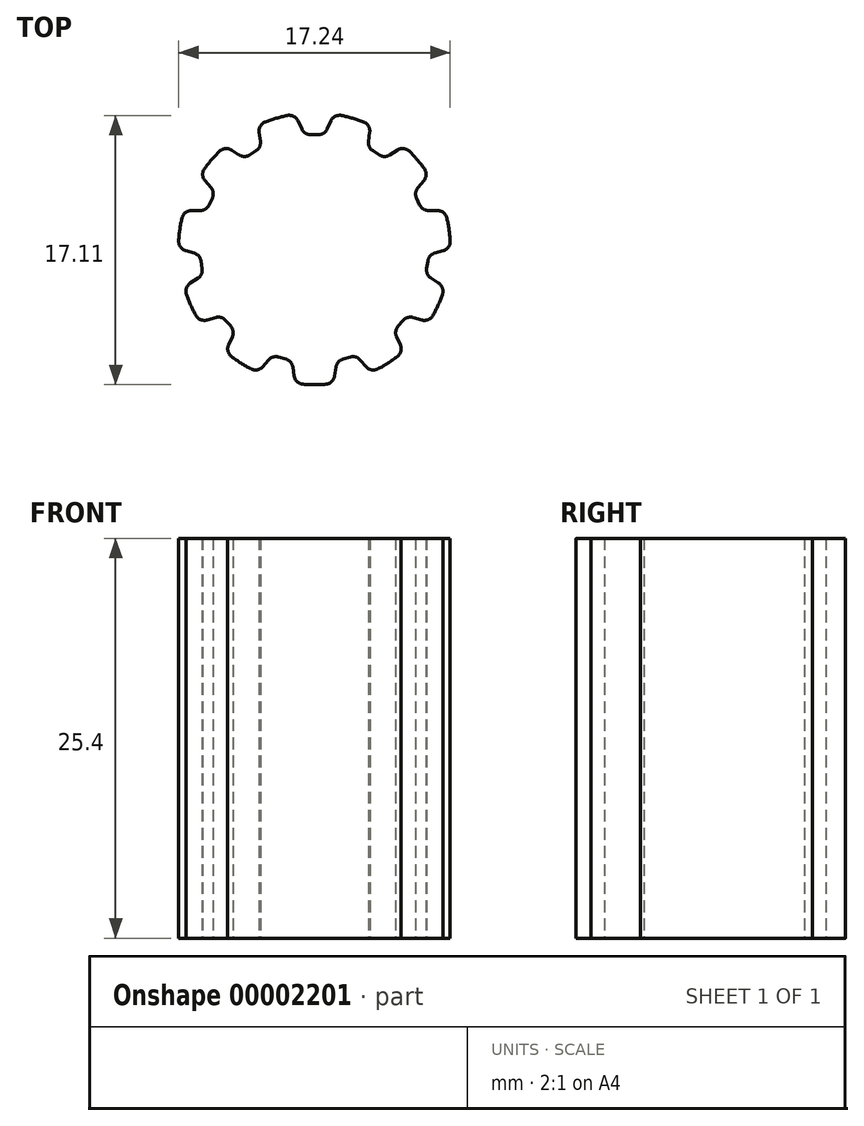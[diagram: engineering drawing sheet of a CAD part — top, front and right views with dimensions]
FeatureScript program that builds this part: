
annotation { "Feature Type Name" : "Feature", "Feature Type Description" : "" }
export const myFeature = defineFeature(function(context is Context, id is Id, definition is map)
    precondition{}
    {
        {
            var Q0;
            Q0=qCreatedBy(makeId("Top.planeOp"),FACE);
            var sketch = newSketch(context, id + "F0", { "sketchPlane" : qUnion([Q0])});
            skArc(sketch, "E0.0.1", {"start": v(8.19, -0.12) * mm, "mid": v(8.51, 0.11) * mm, "end": v(8.62, 0.5) * mm});
            skArc(sketch, "E0.0.3", {"start": v(8.19, -0.12) * mm, "mid": v(8.51, 0.11) * mm, "end": v(8.62, 0.5) * mm});
            skArc(sketch, "E1.1.1", {"start": v(8.41, 1.95) * mm, "mid": v(8.55, 1.23) * mm, "end": v(8.62, 0.5) * mm});
            skArc(sketch, "E1.1.3", {"start": v(8.41, 1.95) * mm, "mid": v(8.55, 1.23) * mm, "end": v(8.62, 0.5) * mm});
            skArc(sketch, "E1.2.1", {"start": v(8.41, 1.95) * mm, "mid": v(8.2, 2.29) * mm, "end": v(7.82, 2.42) * mm});
            skArc(sketch, "E1.2.3", {"start": v(8.41, 1.95) * mm, "mid": v(8.2, 2.29) * mm, "end": v(7.82, 2.42) * mm});
            skArc(sketch, "E1.4.1", {"start": v(6.69, 2.78) * mm, "mid": v(6.91, 2.52) * mm, "end": v(7.24, 2.43) * mm});
            skArc(sketch, "E1.4.3", {"start": v(6.69, 2.78) * mm, "mid": v(6.91, 2.52) * mm, "end": v(7.24, 2.43) * mm});
            skArc(sketch, "E1.6.1", {"start": v(6.57, 3.88) * mm, "mid": v(6.43, 3.57) * mm, "end": v(6.48, 3.23) * mm});
            skArc(sketch, "E1.6.3", {"start": v(6.57, 3.88) * mm, "mid": v(6.43, 3.57) * mm, "end": v(6.48, 3.23) * mm});
            skArc(sketch, "E1.8.1", {"start": v(6.95, 4.33) * mm, "mid": v(7.1, 4.7) * mm, "end": v(6.98, 5.08) * mm});
            skArc(sketch, "E1.8.3", {"start": v(6.95, 4.33) * mm, "mid": v(7.1, 4.7) * mm, "end": v(6.98, 5.08) * mm});
            skArc(sketch, "E1.9.1", {"start": v(6.02, 6.19) * mm, "mid": v(6.53, 5.66) * mm, "end": v(6.98, 5.08) * mm});
            skArc(sketch, "E1.9.3", {"start": v(6.02, 6.19) * mm, "mid": v(6.53, 5.66) * mm, "end": v(6.98, 5.08) * mm});
            skArc(sketch, "E1.10.1", {"start": v(6.02, 6.19) * mm, "mid": v(5.66, 6.36) * mm, "end": v(5.27, 6.27) * mm});
            skArc(sketch, "E1.10.3", {"start": v(6.02, 6.19) * mm, "mid": v(5.66, 6.36) * mm, "end": v(5.27, 6.27) * mm});
            skArc(sketch, "E1.11.1", {"start": v(4.12, 5.96) * mm, "mid": v(4.45, 5.86) * mm, "end": v(4.78, 5.95) * mm});
            skArc(sketch, "E1.11.3", {"start": v(4.12, 5.96) * mm, "mid": v(4.45, 5.86) * mm, "end": v(4.78, 5.95) * mm});
            skArc(sketch, "E1.13.1", {"start": v(3.43, 6.82) * mm, "mid": v(3.48, 6.48) * mm, "end": v(3.7, 6.22) * mm});
            skArc(sketch, "E1.13.3", {"start": v(3.43, 6.82) * mm, "mid": v(3.48, 6.48) * mm, "end": v(3.7, 6.22) * mm});
            skArc(sketch, "E1.15.1", {"start": v(3.51, 7.4) * mm, "mid": v(3.43, 7.8) * mm, "end": v(3.13, 8.05) * mm});
            skArc(sketch, "E1.15.3", {"start": v(3.51, 7.4) * mm, "mid": v(3.43, 7.8) * mm, "end": v(3.13, 8.05) * mm});
            skArc(sketch, "E1.16.1", {"start": v(1.72, 8.46) * mm, "mid": v(2.43, 8.29) * mm, "end": v(3.13, 8.05) * mm});
            skArc(sketch, "E1.16.3", {"start": v(1.72, 8.46) * mm, "mid": v(2.43, 8.29) * mm, "end": v(3.13, 8.05) * mm});
            skArc(sketch, "E1.17.1", {"start": v(1.72, 8.46) * mm, "mid": v(1.33, 8.4) * mm, "end": v(1.05, 8.12) * mm});
            skArc(sketch, "E1.17.3", {"start": v(1.72, 8.46) * mm, "mid": v(1.33, 8.4) * mm, "end": v(1.05, 8.12) * mm});
            skArc(sketch, "E1.19.1", {"start": v(0.25, 7.24) * mm, "mid": v(0.57, 7.33) * mm, "end": v(0.8, 7.6) * mm});
            skArc(sketch, "E1.19.3", {"start": v(0.25, 7.24) * mm, "mid": v(0.57, 7.33) * mm, "end": v(0.8, 7.6) * mm});
            skLineSegment(sketch, "E2.0", {"start": v(7.24, 2.43) * mm, "end": v(7.82, 2.42) * mm});
            skLineSegment(sketch, "E3.0", {"start": v(6.48, 3.23) * mm, "end": v(6.69, 2.78) * mm});
            skLineSegment(sketch, "E4.0", {"start": v(6.95, 4.33) * mm, "end": v(6.57, 3.88) * mm});
            skLineSegment(sketch, "E5.0", {"start": v(3.7, 6.22) * mm, "end": v(4.12, 5.96) * mm});
            skPoint(sketch, "E6.0", {"position": v(3.43, 6.82) * mm});
            skLineSegment(sketch, "E7.0", {"start": v(3.51, 7.4) * mm, "end": v(3.43, 6.82) * mm});
            skLineSegment(sketch, "E8.0", {"start": v(4.78, 5.95) * mm, "end": v(5.27, 6.27) * mm});
            skLineSegment(sketch, "E9.0", {"start": v(0, 7.24) * mm, "end": v(0.25, 7.24) * mm});
            skLineSegment(sketch, "E10.0", {"start": v(0.8, 7.6) * mm, "end": v(1.05, 8.12) * mm});
            skArc(sketch, "E11.0", {"start": v(7.63, -0.29) * mm, "mid": v(7.34, -0.48) * mm, "end": v(7.2, -0.79) * mm});
            skLineSegment(sketch, "E12.0", {"start": v(8.19, -0.12) * mm, "end": v(7.63, -0.29) * mm});
            skLineSegment(sketch, "E13.0", {"start": v(7.2, -0.79) * mm, "end": v(7.13, -1.27) * mm});
            skArc(sketch, "E14.0", {"start": v(7.13, -1.27) * mm, "mid": v(7.18, -1.61) * mm, "end": v(7.4, -1.87) * mm});
            skLineSegment(sketch, "E15.0", {"start": v(7.4, -1.87) * mm, "end": v(7.9, -2.2) * mm});
            skArc(sketch, "E16.0", {"start": v(8.13, -2.9) * mm, "mid": v(8.14, -2.5) * mm, "end": v(7.9, -2.2) * mm});
            skArc(sketch, "E17.0", {"start": v(8.13, -2.9) * mm, "mid": v(7.86, -3.59) * mm, "end": v(7.52, -4.24) * mm});
            skArc(sketch, "E18.0", {"start": v(6.82, -4.53) * mm, "mid": v(7.22, -4.5) * mm, "end": v(7.52, -4.24) * mm});
            skLineSegment(sketch, "E19.0", {"start": v(6.82, -4.53) * mm, "end": v(6.26, -4.37) * mm});
            skArc(sketch, "E20.0", {"start": v(6.26, -4.37) * mm, "mid": v(5.92, -4.37) * mm, "end": v(5.63, -4.55) * mm});
            skLineSegment(sketch, "E21.0", {"start": v(5.63, -4.55) * mm, "end": v(5.3, -4.93) * mm});
            skArc(sketch, "E22.0", {"start": v(5.3, -4.93) * mm, "mid": v(5.17, -5.24) * mm, "end": v(5.21, -5.57) * mm});
            skLineSegment(sketch, "E23.0", {"start": v(5.21, -5.57) * mm, "end": v(5.45, -6.11) * mm});
            skArc(sketch, "E24.0", {"start": v(5.27, -6.84) * mm, "mid": v(5.49, -6.5) * mm, "end": v(5.45, -6.11) * mm});
            skArc(sketch, "E25.0", {"start": v(5.27, -6.84) * mm, "mid": v(4.67, -7.27) * mm, "end": v(4.04, -7.64) * mm});
            skArc(sketch, "E26.0", {"start": v(3.3, -7.5) * mm, "mid": v(3.64, -7.7) * mm, "end": v(4.04, -7.64) * mm});
            skArc(sketch, "E27.0", {"start": v(2.9, -7.06) * mm, "mid": v(2.62, -6.88) * mm, "end": v(2.28, -6.88) * mm});
            skLineSegment(sketch, "E28.0", {"start": v(3.3, -7.5) * mm, "end": v(2.9, -7.06) * mm});
            skLineSegment(sketch, "E29.0", {"start": v(2.28, -6.88) * mm, "end": v(1.8, -7.02) * mm});
            skArc(sketch, "E30.0", {"start": v(1.8, -7.02) * mm, "mid": v(1.52, -7.2) * mm, "end": v(1.37, -7.5) * mm});
            skLineSegment(sketch, "E31.0", {"start": v(1.37, -7.5) * mm, "end": v(1.28, -8.09) * mm});
            skArc(sketch, "E32.0", {"start": v(0.73, -8.6) * mm, "mid": v(1.1, -8.44) * mm, "end": v(1.28, -8.09) * mm});
            skArc(sketch, "E33.0", {"start": v(0.73, -8.6) * mm, "mid": v(0.37, -8.63) * mm, "end": v(0, -8.64) * mm});
            skArc(sketch, "E34.2.MirrorCS", {"start": v(-1.72, 8.46) * mm, "mid": v(-2.43, 8.29) * mm, "end": v(-3.13, 8.05) * mm});
            skArc(sketch, "E34.3.MirrorCS", {"start": v(-8.41, 1.95) * mm, "mid": v(-8.55, 1.23) * mm, "end": v(-8.62, 0.5) * mm});
            skArc(sketch, "E34.4.MirrorCS", {"start": v(-3.43, 6.82) * mm, "mid": v(-3.48, 6.48) * mm, "end": v(-3.7, 6.22) * mm});
            skArc(sketch, "E34.5.MirrorCS", {"start": v(-1.72, 8.46) * mm, "mid": v(-1.33, 8.4) * mm, "end": v(-1.05, 8.12) * mm});
            skArc(sketch, "E34.6.MirrorCS", {"start": v(-4.12, 5.96) * mm, "mid": v(-4.45, 5.86) * mm, "end": v(-4.78, 5.95) * mm});
            skArc(sketch, "E34.7.MirrorCS", {"start": v(-8.19, -0.12) * mm, "mid": v(-8.51, 0.11) * mm, "end": v(-8.62, 0.5) * mm});
            skArc(sketch, "E34.8.MirrorCS", {"start": v(-6.57, 3.88) * mm, "mid": v(-6.43, 3.57) * mm, "end": v(-6.48, 3.23) * mm});
            skArc(sketch, "E34.9.MirrorCS", {"start": v(-3.51, 7.4) * mm, "mid": v(-3.43, 7.8) * mm, "end": v(-3.13, 8.05) * mm});
            skArc(sketch, "E34.10.MirrorCS", {"start": v(-6.69, 2.78) * mm, "mid": v(-6.91, 2.52) * mm, "end": v(-7.24, 2.43) * mm});
            skArc(sketch, "E34.11.MirrorCS", {"start": v(-6.02, 6.19) * mm, "mid": v(-6.53, 5.66) * mm, "end": v(-6.98, 5.08) * mm});
            skArc(sketch, "E34.12.MirrorCS", {"start": v(-6.02, 6.19) * mm, "mid": v(-5.66, 6.36) * mm, "end": v(-5.27, 6.27) * mm});
            skArc(sketch, "E34.13.MirrorCS", {"start": v(-6.95, 4.33) * mm, "mid": v(-7.1, 4.7) * mm, "end": v(-6.98, 5.08) * mm});
            skArc(sketch, "E34.14.MirrorCS", {"start": v(-8.41, 1.95) * mm, "mid": v(-8.2, 2.29) * mm, "end": v(-7.82, 2.42) * mm});
            skArc(sketch, "E34.15.MirrorCS", {"start": v(-8.13, -2.9) * mm, "mid": v(-7.86, -3.59) * mm, "end": v(-7.52, -4.24) * mm});
            skLineSegment(sketch, "E34.16.MirrorCS", {"start": v(-7.4, -1.87) * mm, "end": v(-7.9, -2.2) * mm});
            skPoint(sketch, "E34.18.MirrorP", {"position": v(-3.43, 6.82) * mm});
            skLineSegment(sketch, "E34.19.MirrorCS", {"start": v(-6.82, -4.53) * mm, "end": v(-6.26, -4.37) * mm});
            skArc(sketch, "E34.20.MirrorCS", {"start": v(-8.13, -2.9) * mm, "mid": v(-8.14, -2.5) * mm, "end": v(-7.9, -2.2) * mm});
            skArc(sketch, "E34.21.MirrorCS", {"start": v(-5.3, -4.93) * mm, "mid": v(-5.17, -5.24) * mm, "end": v(-5.21, -5.57) * mm});
            skLineSegment(sketch, "E34.22.MirrorCS", {"start": v(-8.19, -0.12) * mm, "end": v(-7.63, -0.29) * mm});
            skLineSegment(sketch, "E34.23.MirrorCS", {"start": v(-3.3, -7.5) * mm, "end": v(-2.9, -7.06) * mm});
            skArc(sketch, "E34.24.MirrorCS", {"start": v(-3.51, 7.4) * mm, "mid": v(-3.43, 7.8) * mm, "end": v(-3.13, 8.05) * mm});
            skArc(sketch, "E34.25.MirrorCS", {"start": v(-1.72, 8.46) * mm, "mid": v(-2.43, 8.29) * mm, "end": v(-3.13, 8.05) * mm});
            skArc(sketch, "E34.26.MirrorCS", {"start": v(-6.57, 3.88) * mm, "mid": v(-6.43, 3.57) * mm, "end": v(-6.48, 3.23) * mm});
            skLineSegment(sketch, "E34.27.MirrorCS", {"start": v(-6.48, 3.23) * mm, "end": v(-6.69, 2.78) * mm});
            skArc(sketch, "E34.28.MirrorCS", {"start": v(-5.27, -6.84) * mm, "mid": v(-5.49, -6.5) * mm, "end": v(-5.45, -6.11) * mm});
            skArc(sketch, "E34.29.MirrorCS", {"start": v(-4.12, 5.96) * mm, "mid": v(-4.45, 5.86) * mm, "end": v(-4.78, 5.95) * mm});
            skLineSegment(sketch, "E34.30.MirrorCS", {"start": v(-5.63, -4.55) * mm, "end": v(-5.3, -4.93) * mm});
            skLineSegment(sketch, "E34.31.MirrorCS", {"start": v(-3.7, 6.22) * mm, "end": v(-4.12, 5.96) * mm});
            skArc(sketch, "E34.32.MirrorCS", {"start": v(-6.02, 6.19) * mm, "mid": v(-6.53, 5.66) * mm, "end": v(-6.98, 5.08) * mm});
            skLineSegment(sketch, "E34.33.MirrorCS", {"start": v(-5.21, -5.57) * mm, "end": v(-5.45, -6.11) * mm});
            skArc(sketch, "E34.34.MirrorCS", {"start": v(-6.26, -4.37) * mm, "mid": v(-5.92, -4.37) * mm, "end": v(-5.63, -4.55) * mm});
            skArc(sketch, "E34.35.MirrorCS", {"start": v(-1.72, 8.46) * mm, "mid": v(-1.33, 8.4) * mm, "end": v(-1.05, 8.12) * mm});
            skArc(sketch, "E34.36.MirrorCS", {"start": v(-8.41, 1.95) * mm, "mid": v(-8.55, 1.23) * mm, "end": v(-8.62, 0.5) * mm});
            skLineSegment(sketch, "E34.37.MirrorCS", {"start": v(-2.28, -6.88) * mm, "end": v(-1.8, -7.02) * mm});
            skArc(sketch, "E34.38.MirrorCS", {"start": v(-3.3, -7.5) * mm, "mid": v(-3.64, -7.7) * mm, "end": v(-4.04, -7.64) * mm});
            skArc(sketch, "E34.39.MirrorCS", {"start": v(-6.02, 6.19) * mm, "mid": v(-5.66, 6.36) * mm, "end": v(-5.27, 6.27) * mm});
            skArc(sketch, "E34.40.MirrorCS", {"start": v(-8.41, 1.95) * mm, "mid": v(-8.2, 2.29) * mm, "end": v(-7.82, 2.42) * mm});
            skLineSegment(sketch, "E34.41.MirrorCS", {"start": v(-4.78, 5.95) * mm, "end": v(-5.27, 6.27) * mm});
            skLineSegment(sketch, "E34.42.MirrorCS", {"start": v(-3.51, 7.4) * mm, "end": v(-3.43, 6.82) * mm});
            skArc(sketch, "E34.43.MirrorCS", {"start": v(-7.13, -1.27) * mm, "mid": v(-7.18, -1.61) * mm, "end": v(-7.4, -1.87) * mm});
            skArc(sketch, "E34.44.MirrorCS", {"start": v(-7.63, -0.29) * mm, "mid": v(-7.34, -0.48) * mm, "end": v(-7.2, -0.79) * mm});
            skArc(sketch, "E34.45.MirrorCS", {"start": v(-2.9, -7.06) * mm, "mid": v(-2.62, -6.88) * mm, "end": v(-2.28, -6.88) * mm});
            skLineSegment(sketch, "E34.46.MirrorCS", {"start": v(-1.37, -7.5) * mm, "end": v(-1.28, -8.09) * mm});
            skArc(sketch, "E34.48.MirrorCS", {"start": v(-1.8, -7.02) * mm, "mid": v(-1.52, -7.2) * mm, "end": v(-1.37, -7.5) * mm});
            skLineSegment(sketch, "E34.49.MirrorCS", {"start": v(-7.2, -0.79) * mm, "end": v(-7.13, -1.27) * mm});
            skArc(sketch, "E34.50.MirrorCS", {"start": v(-6.82, -4.53) * mm, "mid": v(-7.22, -4.5) * mm, "end": v(-7.52, -4.24) * mm});
            skLineSegment(sketch, "E34.51.MirrorCS", {"start": v(-7.24, 2.43) * mm, "end": v(-7.82, 2.42) * mm});
            skArc(sketch, "E34.52.MirrorCS", {"start": v(-3.43, 6.82) * mm, "mid": v(-3.48, 6.48) * mm, "end": v(-3.7, 6.22) * mm});
            skArc(sketch, "E34.53.MirrorCS", {"start": v(-5.27, -6.84) * mm, "mid": v(-4.67, -7.27) * mm, "end": v(-4.04, -7.64) * mm});
            skLineSegment(sketch, "E34.55.MirrorCS", {"start": v(-6.95, 4.33) * mm, "end": v(-6.57, 3.88) * mm});
            skArc(sketch, "E35.0.MirrorCS", {"start": v(-0.73, -8.6) * mm, "mid": v(-1.1, -8.44) * mm, "end": v(-1.28, -8.09) * mm});
            skArc(sketch, "E36.0.MirrorCS", {"start": v(-0.73, -8.6) * mm, "mid": v(-0.37, -8.63) * mm, "end": v(0, -8.64) * mm});
            skLineSegment(sketch, "E37.0.MirrorCS", {"start": v(-0.8, 7.6) * mm, "end": v(-1.05, 8.12) * mm});
            skArc(sketch, "E38.0.MirrorCS", {"start": v(-0.25, 7.24) * mm, "mid": v(-0.57, 7.33) * mm, "end": v(-0.8, 7.6) * mm});
            skLineSegment(sketch, "E39.0.MirrorCS", {"start": v(0, 7.24) * mm, "end": v(-0.25, 7.24) * mm});
            skSolve(sketch);
        }
        {
            var Q0;
            Q0 = qSketchRegion(id + "F0", true);
            extrude(context, id + "F1", {"entities" : qUnion([Q0]), "depth" : 25.4 * mm});
        }
    });
